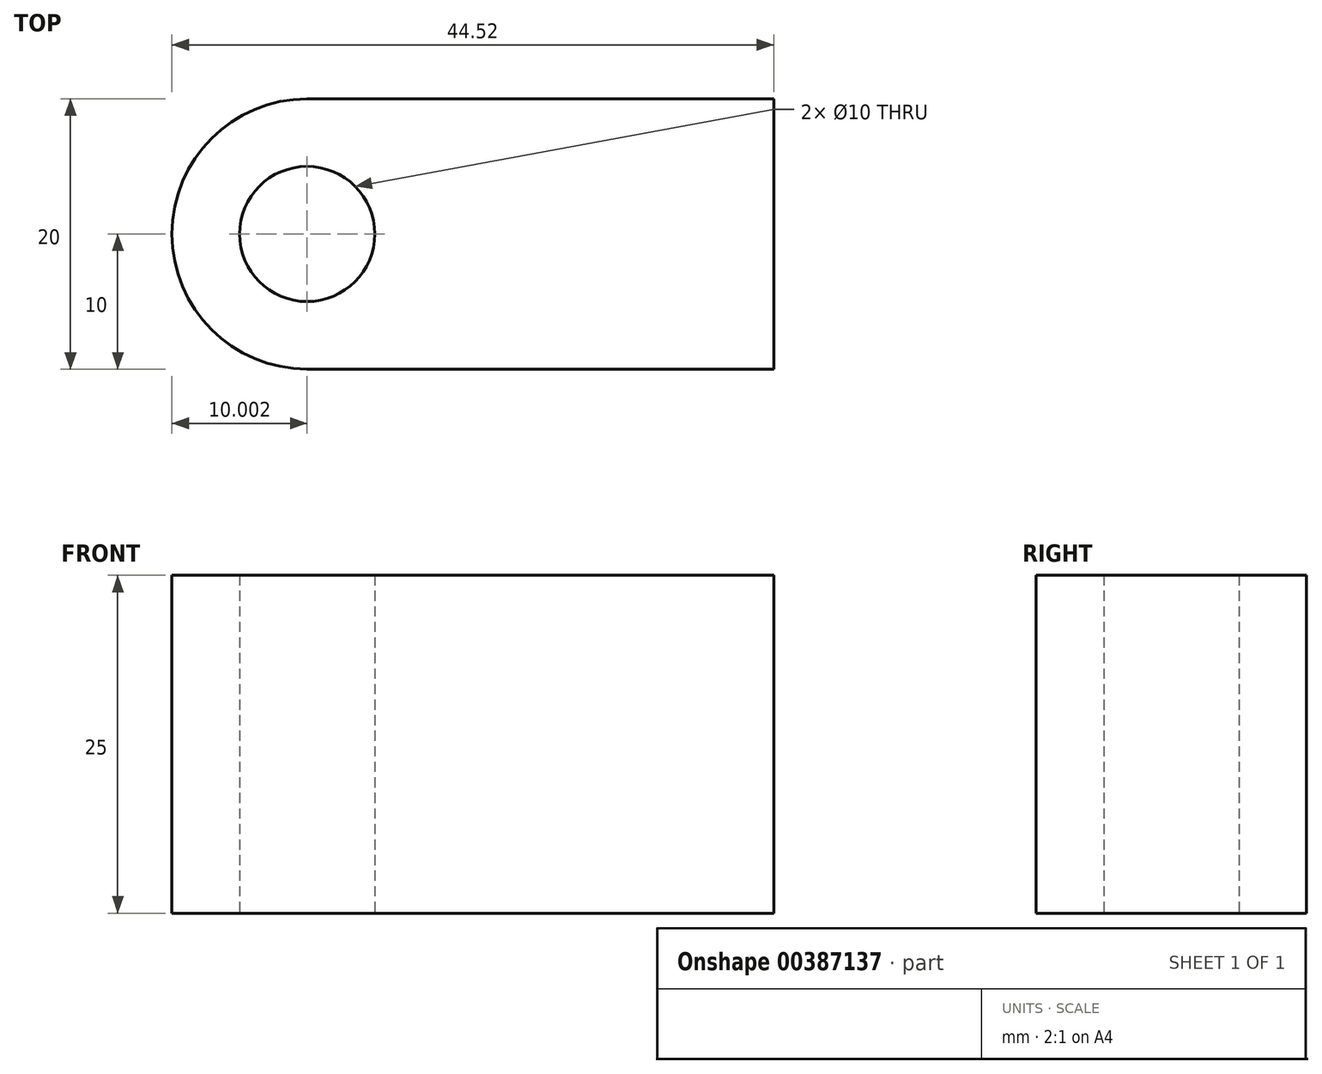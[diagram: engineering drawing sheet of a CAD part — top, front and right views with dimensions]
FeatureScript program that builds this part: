
annotation { "Feature Type Name" : "Feature", "Feature Type Description" : "" }
export const myFeature = defineFeature(function(context is Context, id is Id, definition is map)
    precondition{}
    {
        {
            var Q0;
            Q0=qCreatedBy(makeId("Top.planeOp"),FACE);
            var sketch = newSketch(context, id + "F0", { "sketchPlane" : qUnion([Q0])});
            skLineSegment(sketch, "E0.bottom", {"start": v(17.26, -10) * mm, "end": v(-17.26, -10) * mm});
            skLineSegment(sketch, "E0.top", {"start": v(17.26, 10) * mm, "end": v(-17.26, 10) * mm});
            skLineSegment(sketch, "E0.left", {"start": v(17.26, -10) * mm, "end": v(17.26, 10) * mm});
            skLineSegment(sketch, "E0.right", {"start": v(-17.26, -10) * mm, "end": v(-17.26, 10) * mm});
            skPoint(sketch, "E0.middle", {"position": v(0, 0) * mm});
            skCircle(sketch, "E1", {"center": v(-17.26, 0) * mm, "radius": 10 * mm});
            skCircle(sketch, "E2", {"center": v(-17.26, 0) * mm, "radius": 5 * mm});
            skSolve(sketch);
        }
        {
            var Q0;
            {var subQ0=sQuery(id+"F0.wireOp",EDGE,"E0.bottom");Q0=makeQuery(id+"F0.imprint","IMPRINT",FACE,{"disambiguationData":[TD([[makeQuery(id+"F0.imprint","IMPRINT",EDGE,{"derivedFrom":subQ0}),-1.0]])]});}
            var Q1;
            {var subQ0=sQuery(id+"F0.wireOp",EDGE,"E2");var subQ1=sQuery(id+"F0.wireOp",EDGE,"E0.right");var subQ2=makeQuery(id+"F0.imprint","INTERSECT",VERTEX,{"disambiguationData":[OD(0.0)],"derivedFrom":[subQ1,subQ0]});Q1=makeQuery(id+"F0.imprint","IMPRINT",FACE,{"disambiguationData":[TD([[makeQuery(id+"F0.imprint","IMPRINT",EDGE,{"disambiguationData":[TD([[subQ2,-1.0]])],"derivedFrom":subQ1}),-1.0]])]});}
            var Q2;
            {var subQ0=sQuery(id+"F0.wireOp",EDGE,"E2");var subQ1=sQuery(id+"F0.wireOp",EDGE,"E0.right");var subQ2=makeQuery(id+"F0.imprint","INTERSECT",VERTEX,{"disambiguationData":[OD(0.0)],"derivedFrom":[subQ1,subQ0]});Q2=makeQuery(id+"F0.imprint","IMPRINT",FACE,{"disambiguationData":[TD([[makeQuery(id+"F0.imprint","IMPRINT",EDGE,{"disambiguationData":[TD([[subQ2,-1.0]])],"derivedFrom":subQ1}),1.0]])]});}
            var Q3;
            {var subQ1=sQuery(id+"F0.wireOp",EDGE,"E0.right");var subQ3=sQuery(id+"F0.wireOp",EDGE,"E2");var subQ4=makeQuery(id+"F0.imprint","INTERSECT",VERTEX,{"disambiguationData":[OD(0.0)],"derivedFrom":[subQ1,subQ3]});Q3=makeQuery(id+"F0.imprint","IMPRINT",FACE,{"disambiguationData":[TD([[makeQuery(id+"F0.imprint","IMPRINT",EDGE,{"disambiguationData":[TD([[subQ4,1.0]])],"derivedFrom":subQ3}),-1.0]])]});}
            var Q4;
            {var subQ1=sQuery(id+"F0.wireOp",EDGE,"E0.right");var subQ3=sQuery(id+"F0.wireOp",EDGE,"E2");var subQ4=makeQuery(id+"F0.imprint","INTERSECT",VERTEX,{"disambiguationData":[OD(0.0)],"derivedFrom":[subQ1,subQ3]});Q4=makeQuery(id+"F0.imprint","IMPRINT",FACE,{"disambiguationData":[TD([[makeQuery(id+"F0.imprint","IMPRINT",EDGE,{"disambiguationData":[TD([[subQ4,-1.0]])],"derivedFrom":subQ3}),-1.0]])]});}
            extrude(context, id + "F1", {"entities" : qUnion([Q0, Q1, Q2, Q3, Q4]), "depth" : 25 * mm});
        }
    });
